FCSTD DOCUMENT  (FreeCAD 0.20R26155 (Git))
Label: D3SH
License: All rights reserved
LicenseURL: http://en.wikipedia.org/wiki/All_rights_reserved
objects: Sketcher::SketchObject×3, PartDesign::Body×1
note: 4 computed .brp shape members not serialized (recipe doc carries the construction recipe); baked Part::Feature solids carry a one-line shape summary decoded from their .brp

FEATURE [PartDesign::Body] Body
  Origin = -> Origin
FEATURE [Sketcher::SketchObject] Sketch  label="Pads_TH_SMD"
  FullyConstrained = false
  MapMode = 5
  Support = -> [XY_Plane]
  sketch-geometry (13):
    g0: LineSegment StartX=-2.2 StartY=2.2 StartZ=0 EndX=-1.1 EndY=2.2 EndZ=0
    g1: LineSegment StartX=-1.1 StartY=2.2 StartZ=0 EndX=-1.1 EndY=1.1 EndZ=0
    g2: LineSegment StartX=-1.1 StartY=1.1 StartZ=0 EndX=-2.2 EndY=1.1 EndZ=0
    g3: LineSegment StartX=-2.2 StartY=1.1 StartZ=0 EndX=-2.2 EndY=2.2 EndZ=0
    g4: LineSegment StartX=2.2 StartY=2.05 StartZ=0 EndX=1.1 EndY=2.05 EndZ=0
    g5: LineSegment StartX=1.1 StartY=2.05 StartZ=0 EndX=1.1 EndY=1.1 EndZ=0
    g6: LineSegment StartX=1.1 StartY=1.1 StartZ=0 EndX=2.2 EndY=1.1 EndZ=0
    g7: LineSegment StartX=2.2 StartY=1.1 StartZ=0 EndX=2.2 EndY=2.05 EndZ=0
    g8: Circle CenterX=0 CenterY=2.8 CenterZ=0 NormalX=0 NormalY=0 NormalZ=1 AngleXU=0 Radius=0.35
    g9: Circle CenterX=0 CenterY=0.8 CenterZ=0 NormalX=0 NormalY=0 NormalZ=1 AngleXU=0 Radius=0.35
    g10: LineSegment StartX=-1.23996 StartY=0 StartZ=0 EndX=1.52331 EndY=0 EndZ=0
    g11: LineSegment StartX=1.1 StartY=1.65 StartZ=0 EndX=2.2 EndY=1.65 EndZ=0
    g12: LineSegment StartX=1.1 StartY=1.65 StartZ=0 EndX=-2.2 EndY=1.65 EndZ=0
  constraints (37):
    c: Coincident(g0,g1)
    c: Coincident(g1,g2)
    c: Coincident(g2,g3)
    c: Coincident(g3,g0)
    c: Horizontal(g0)
    c: Horizontal(g2)
    c: Vertical(g1)
    c: Vertical(g3)
    c: Coincident(g4,g5)
    c: Coincident(g5,g6)
    c: Coincident(g6,g7)
    c: Coincident(g7,g4)
    c: Horizontal(g4)
    c: Horizontal(g6)
    c: Vertical(g5)
    c: Vertical(g7)
    c: PointOnObject(g8,g-2)
    c: PointOnObject(g9,g-2)
    c: Equal(g9,g8)
    c: Radius(g8) = 0.35
    c: DistanceY(g9,g8) = 2
    c: DistanceY(g3,g3) = 1.1
    c: DistanceX(g1,g5) = 2.2
    c: DistanceX(g2,g6) = 4.4
    c: Symmetric(g1,g5,g-2)
    c: Equal(g2,g6)
    c: Horizontal(g10)
    c: DistanceY(g10,g8) = 2.8
    c: PointOnObject(g11,g5)
    c: PointOnObject(g11,g7)
    c: Horizontal(g11)
    c: DistanceY(g11,g4) = 0.4
    c: DistanceY(g6,g11) = 0.55
    c: DistanceY(g10,g11) = 1.65
    c: Coincident(g12,g11)
    c: Symmetric(g3,g3,g12)
    c: PointOnObject(g10,g-1)
FEATURE [Sketcher::SketchObject] Sketch001  label="Edge_Cuts_0.15"
  FullyConstrained = false
  MapMode = 5
  Support = -> [XY_Plane]
  sketch-geometry (13):
    g0: LineSegment StartX=-2.2 StartY=2.2 StartZ=0 EndX=-1.1 EndY=2.2 EndZ=0
    g1: LineSegment StartX=-1.1 StartY=2.2 StartZ=0 EndX=-1.1 EndY=1.1 EndZ=0
    g2: LineSegment StartX=-1.1 StartY=1.1 StartZ=0 EndX=-2.2 EndY=1.1 EndZ=0
    g3: LineSegment StartX=-2.2 StartY=1.1 StartZ=0 EndX=-2.2 EndY=2.2 EndZ=0
    g4: LineSegment StartX=2.2 StartY=2.05 StartZ=0 EndX=1.1 EndY=2.05 EndZ=0
    g5: LineSegment StartX=1.1 StartY=2.05 StartZ=0 EndX=1.1 EndY=1.1 EndZ=0
    g6: LineSegment StartX=1.1 StartY=1.1 StartZ=0 EndX=2.2 EndY=1.1 EndZ=0
    g7: LineSegment StartX=2.2 StartY=1.1 StartZ=0 EndX=2.2 EndY=2.05 EndZ=0
    g8: Circle CenterX=0 CenterY=2.8 CenterZ=0 NormalX=0 NormalY=0 NormalZ=1 AngleXU=0 Radius=0.35
    g9: Circle CenterX=0 CenterY=0.8 CenterZ=0 NormalX=0 NormalY=0 NormalZ=1 AngleXU=0 Radius=0.35
    g10: LineSegment StartX=-1.23996 StartY=0 StartZ=0 EndX=1.52331 EndY=0 EndZ=0
    g11: LineSegment StartX=1.1 StartY=1.65 StartZ=0 EndX=2.2 EndY=1.65 EndZ=0
    g12: LineSegment StartX=1.1 StartY=1.65 StartZ=0 EndX=-2.2 EndY=1.65 EndZ=0
  constraints (37):
    c: Coincident(g0,g1)
    c: Coincident(g1,g2)
    c: Coincident(g2,g3)
    c: Coincident(g3,g0)
    c: Horizontal(g0)
    c: Horizontal(g2)
    c: Vertical(g1)
    c: Vertical(g3)
    c: Coincident(g4,g5)
    c: Coincident(g5,g6)
    c: Coincident(g6,g7)
    c: Coincident(g7,g4)
    c: Horizontal(g4)
    c: Horizontal(g6)
    c: Vertical(g5)
    c: Vertical(g7)
    c: PointOnObject(g8,g-2)
    c: PointOnObject(g9,g-2)
    c: Equal(g9,g8)
    c: Radius(g8) = 0.35
    c: DistanceY(g9,g8) = 2
    c: DistanceY(g3,g3) = 1.1
    c: DistanceX(g1,g5) = 2.2
    c: DistanceX(g2,g6) = 4.4
    c: Symmetric(g1,g5,g-2)
    c: Equal(g2,g6)
    c: Horizontal(g10)
    c: DistanceY(g10,g8) = 2.8
    c: PointOnObject(g11,g5)
    c: PointOnObject(g11,g7)
    c: Horizontal(g11)
    c: DistanceY(g11,g4) = 0.4
    c: DistanceY(g6,g11) = 0.55
    c: DistanceY(g10,g11) = 1.65
    c: Coincident(g12,g11)
    c: Symmetric(g3,g3,g12)
    c: PointOnObject(g10,g-1)
FEATURE [Sketcher::SketchObject] Sketch002  label="F_CrtYd_0.1"
  ExternalGeometry = -> [Sketch001,Sketch]
  FullyConstrained = true
  MapMode = 5
  Support = -> [XY_Plane]
  sketch-geometry (5):
    g0: LineSegment StartX=-1.5 StartY=3.725 StartZ=0 EndX=1.5 EndY=3.725 EndZ=0
    g1: LineSegment StartX=1.5 StartY=3.725 StartZ=0 EndX=1.5 EndY=-0.075 EndZ=0
    g2: LineSegment StartX=1.5 StartY=-0.075 StartZ=0 EndX=-1.5 EndY=-0.075 EndZ=0
    g3: LineSegment StartX=-1.5 StartY=-0.075 StartZ=0 EndX=-1.5 EndY=3.725 EndZ=0
    g4: GeomPoint X=2.2 Y=1.575 Z=0
  constraints (12):
    c: Coincident(g0,g1)
    c: Coincident(g1,g2)
    c: Coincident(g2,g3)
    c: Coincident(g3,g0)
    c: Horizontal(g0)
    c: Vertical(g1)
    c: Vertical(g3)
    c: Symmetric(g1,g2,g-2)
    c: DistanceX(g2,g2) = 3
    c: DistanceY(g1,g1) = 3.8
    c: Symmetric(g-4,g-4,g4)
    c: DistanceY(g1,g4) = 1.65
